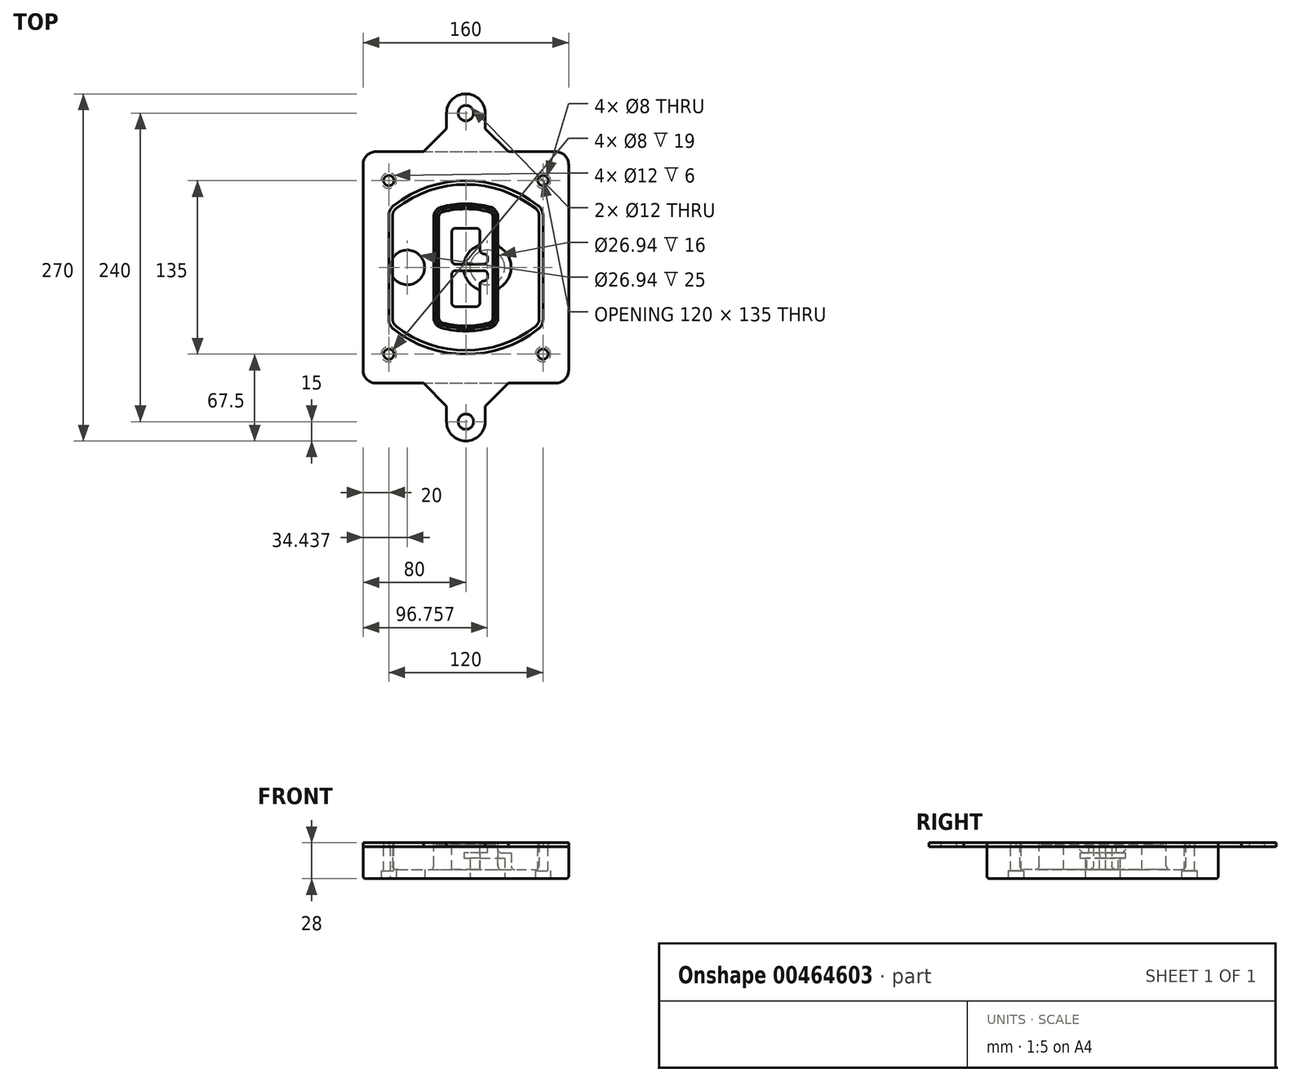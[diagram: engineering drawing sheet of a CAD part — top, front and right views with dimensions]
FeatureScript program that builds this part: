
annotation { "Feature Type Name" : "Feature", "Feature Type Description" : "" }
export const myFeature = defineFeature(function(context is Context, id is Id, definition is map)
    precondition{}
    {
        {
            var Q0;
            Q0=qCreatedBy(makeId("Top.planeOp"),FACE);
            var sketch = newSketch(context, id + "F0", { "sketchPlane" : qUnion([Q0])});
            skPoint(sketch, "E0.rect.middle", {"position": v(0, 0) * mm});
            skLineSegment(sketch, "E1.bottom", {"start": v(-70, -90) * mm, "end": v(70, -90) * mm});
            skLineSegment(sketch, "E1.top", {"start": v(-70, 90) * mm, "end": v(70, 90) * mm});
            skLineSegment(sketch, "E1.left", {"start": v(-80, -80) * mm, "end": v(-80, 80) * mm});
            skLineSegment(sketch, "E1.right", {"start": v(80, -80) * mm, "end": v(80, 80) * mm});
            skLineSegment(sketch, "E2", {"start": v(-80, 90) * mm, "end": v(80, -90) * mm, "construction": true});
            skLineSegment(sketch, "E3", {"start": v(80, 90) * mm, "end": v(-80, -90) * mm, "construction": true});
            skCircle(sketch, "E4", {"center": v(-60, 67.5) * mm, "radius": 4 * mm});
            skCircle(sketch, "E5", {"center": v(60, 67.5) * mm, "radius": 4 * mm});
            skCircle(sketch, "E6", {"center": v(60, -67.5) * mm, "radius": 4 * mm});
            skCircle(sketch, "E7", {"center": v(-60, -67.5) * mm, "radius": 4 * mm});
            skLineSegment(sketch, "E8", {"start": v(-60, 67.5) * mm, "end": v(60, 67.5) * mm, "construction": true});
            skLineSegment(sketch, "E9", {"start": v(60, 67.5) * mm, "end": v(60, -67.5) * mm, "construction": true});
            skLineSegment(sketch, "E10", {"start": v(60, -67.5) * mm, "end": v(-60, -67.5) * mm, "construction": true});
            skLineSegment(sketch, "E11", {"start": v(-60, -67.5) * mm, "end": v(-60, 67.5) * mm, "construction": true});
            skLineSegment(sketch, "E12", {"start": v(-60, 40.3) * mm, "end": v(-60, -40.3) * mm});
            skLineSegment(sketch, "E13", {"start": v(60, 40.3) * mm, "end": v(60, -40.3) * mm});
            skArc(sketch, "E14", {"start": v(56.15, 48.18) * mm, "mid": v(0, 67.5) * mm, "end": v(-56.15, 48.18) * mm});
            skArc(sketch, "E15", {"start": v(-56.15, -48.18) * mm, "mid": v(0, -67.5) * mm, "end": v(56.15, -48.18) * mm});
            skLineSegment(sketch, "E16", {"start": v(-60, 0) * mm, "end": v(60, 0) * mm, "construction": true});
            skPoint(sketch, "E17.visualSharp", {"position": v(-60, -45) * mm});
            skArc(sketch, "E17.filletArc", {"start": v(-60, -40.3) * mm, "mid": v(-58.99, -44.68) * mm, "end": v(-56.15, -48.18) * mm});
            skPoint(sketch, "E18.visualSharp", {"position": v(-60, 45) * mm});
            skArc(sketch, "E18.filletArc", {"start": v(-56.15, 48.18) * mm, "mid": v(-58.99, 44.68) * mm, "end": v(-60, 40.3) * mm});
            skPoint(sketch, "E19.visualSharp", {"position": v(60, 45) * mm});
            skArc(sketch, "E19.filletArc", {"start": v(60, 40.3) * mm, "mid": v(58.99, 44.68) * mm, "end": v(56.15, 48.18) * mm});
            skPoint(sketch, "E20.visualSharp", {"position": v(60, -45) * mm});
            skArc(sketch, "E20.filletArc", {"start": v(56.15, -48.18) * mm, "mid": v(58.99, -44.68) * mm, "end": v(60, -40.3) * mm});
            skPoint(sketch, "E21.visualSharp", {"position": v(-80, 90) * mm});
            skArc(sketch, "E21.filletArc", {"start": v(-70, 90) * mm, "mid": v(-77.07, 87.07) * mm, "end": v(-80, 80) * mm});
            skPoint(sketch, "E22.visualSharp", {"position": v(80, 90) * mm});
            skArc(sketch, "E22.filletArc", {"start": v(80, 80) * mm, "mid": v(77.07, 87.07) * mm, "end": v(70, 90) * mm});
            skPoint(sketch, "E23.visualSharp", {"position": v(80, -90) * mm});
            skArc(sketch, "E23.filletArc", {"start": v(70, -90) * mm, "mid": v(77.07, -87.07) * mm, "end": v(80, -80) * mm});
            skPoint(sketch, "E24.visualSharp", {"position": v(-80, -90) * mm});
            skArc(sketch, "E24.filletArc", {"start": v(-80, -80) * mm, "mid": v(-77.07, -87.07) * mm, "end": v(-70, -90) * mm});
            skArc(sketch, "E25.0", {"start": v(57, 40.3) * mm, "mid": v(56.3, 43.36) * mm, "end": v(54.3, 45.81) * mm});
            skLineSegment(sketch, "E25.1", {"start": v(57, 40.3) * mm, "end": v(57, -40.3) * mm});
            skArc(sketch, "E25.2", {"start": v(54.3, -45.81) * mm, "mid": v(56.3, -43.36) * mm, "end": v(57, -40.3) * mm});
            skArc(sketch, "E25.3", {"start": v(-54.3, -45.81) * mm, "mid": v(0, -64.5) * mm, "end": v(54.3, -45.81) * mm});
            skArc(sketch, "E25.4", {"start": v(-57, -40.3) * mm, "mid": v(-56.3, -43.36) * mm, "end": v(-54.3, -45.81) * mm});
            skArc(sketch, "E25.5", {"start": v(54.3, 45.81) * mm, "mid": v(0, 64.5) * mm, "end": v(-54.3, 45.81) * mm});
            skLineSegment(sketch, "E25.6", {"start": v(-57, 40.3) * mm, "end": v(-57, -40.3) * mm});
            skArc(sketch, "E25.7", {"start": v(-54.3, 45.81) * mm, "mid": v(-56.3, 43.36) * mm, "end": v(-57, 40.3) * mm});
            skArc(sketch, "E26.0", {"start": v(-58.62, 51.33) * mm, "mid": v(-62.58, 46.43) * mm, "end": v(-64, 40.3) * mm});
            skArc(sketch, "E26.1", {"start": v(58.62, 51.33) * mm, "mid": v(0, 71.5) * mm, "end": v(-58.62, 51.33) * mm});
            skArc(sketch, "E26.2", {"start": v(64, 40.3) * mm, "mid": v(62.58, 46.43) * mm, "end": v(58.62, 51.33) * mm});
            skLineSegment(sketch, "E26.3", {"start": v(64, 40.3) * mm, "end": v(64, -40.3) * mm});
            skArc(sketch, "E26.4", {"start": v(58.62, -51.33) * mm, "mid": v(62.58, -46.43) * mm, "end": v(64, -40.3) * mm});
            skLineSegment(sketch, "E26.5", {"start": v(-64, 40.3) * mm, "end": v(-64, -40.3) * mm});
            skArc(sketch, "E26.6", {"start": v(-58.62, -51.33) * mm, "mid": v(0, -71.5) * mm, "end": v(58.62, -51.33) * mm});
            skArc(sketch, "E26.7", {"start": v(-64, -40.3) * mm, "mid": v(-62.58, -46.43) * mm, "end": v(-58.62, -51.33) * mm});
            skSolve(sketch);
        }
        {
            var Q0;
            Q0=makeQuery(id+"F0.imprint","IMPRINT",FACE,{"disambiguationData":[TD([[makeQuery(id+"F0.imprint","IMPRINT",EDGE,{"derivedFrom":sQuery(id+"F0.wireOp",EDGE,"E1.bottom")}),1.0]])]});
            var Q1;
            Q1=makeQuery(id+"F0.imprint","IMPRINT",FACE,{"disambiguationData":[TD([[makeQuery(id+"F0.imprint","IMPRINT",EDGE,{"derivedFrom":sQuery(id+"F0.wireOp",EDGE,"E12")}),1.0]])]});
            var Q2;
            Q2=makeQuery(id+"F0.imprint","IMPRINT",FACE,{"disambiguationData":[TD([[makeQuery(id+"F0.imprint","IMPRINT",EDGE,{"derivedFrom":sQuery(id+"F0.wireOp",EDGE,"E25.0")}),1.0]])]});
            var Q3;
            Q3=makeQuery(id+"F0.imprint","IMPRINT",FACE,{"disambiguationData":[TD([[makeQuery(id+"F0.imprint","IMPRINT",EDGE,{"derivedFrom":sQuery(id+"F0.wireOp",EDGE,"E12")}),-1.0]])]});
            extrude(context, id + "F1", {"entities" : qUnion([Q0, Q1, Q2, Q3]), "oppositeDirection" : true, "depth" : 25 * mm});
        }
        {
            var Q0;
            Q0=makeQuery(id+"F0.imprint","IMPRINT",FACE,{"disambiguationData":[TD([[makeQuery(id+"F0.imprint","IMPRINT",EDGE,{"derivedFrom":sQuery(id+"F0.wireOp",EDGE,"E12")}),1.0]])]});
            extrude(context, id + "F2", {"entities" : qUnion([Q0]), "operationType" : NewBodyOperationType.ADD, "depth" : 3 * mm});
        }
        {
            var Q0;
            Q0=makeQuery(id+"F0.imprint","IMPRINT",FACE,{"disambiguationData":[TD([[makeQuery(id+"F0.imprint","IMPRINT",EDGE,{"derivedFrom":sQuery(id+"F0.wireOp",EDGE,"E25.0")}),1.0]])]});
            extrude(context, id + "F3", {"entities" : qUnion([Q0]), "operationType" : NewBodyOperationType.REMOVE, "oppositeDirection" : true, "depth" : 18 * mm});
        }
        {
            var Q0;
            Q0=makeQuery(id+"F2.opExtrude","CAP_FACE",FACE,{"disambiguationData":[OSD([sQuery(id+"F0.wireOp",EDGE,"E12"),sQuery(id+"F0.wireOp",EDGE,"E13"),sQuery(id+"F0.wireOp",EDGE,"E14"),sQuery(id+"F0.wireOp",EDGE,"E15"),sQuery(id+"F0.wireOp",EDGE,"E17.filletArc"),sQuery(id+"F0.wireOp",EDGE,"E18.filletArc"),sQuery(id+"F0.wireOp",EDGE,"E19.filletArc"),sQuery(id+"F0.wireOp",EDGE,"E20.filletArc"),sQuery(id+"F0.wireOp",EDGE,"E25.0"),sQuery(id+"F0.wireOp",EDGE,"E25.1"),sQuery(id+"F0.wireOp",EDGE,"E25.2"),sQuery(id+"F0.wireOp",EDGE,"E25.3"),sQuery(id+"F0.wireOp",EDGE,"E25.4"),sQuery(id+"F0.wireOp",EDGE,"E25.5"),sQuery(id+"F0.wireOp",EDGE,"E25.6"),sQuery(id+"F0.wireOp",EDGE,"E25.7")])],"isStart":false});
            var sketch = newSketch(context, id + "F4", { "sketchPlane" : qUnion([Q0])});
            skArc(sketch, "E27.0", {"start": v(-19.08, -46.97) * mm, "mid": v(0, -49.5) * mm, "end": v(19.08, -46.97) * mm});
            skArc(sketch, "E28.0", {"start": v(19.08, 46.97) * mm, "mid": v(0, 49.5) * mm, "end": v(-19.08, 46.97) * mm});
            skLineSegment(sketch, "E29", {"start": v(-25, 39.25) * mm, "end": v(-25, -39.25) * mm});
            skLineSegment(sketch, "E30", {"start": v(25, 39.25) * mm, "end": v(25, -39.25) * mm});
            skLineSegment(sketch, "E31", {"start": v(-25, 45.1) * mm, "end": v(25, 45.1) * mm, "construction": true});
            skLineSegment(sketch, "E32", {"start": v(-25, -45.1) * mm, "end": v(25, -45.1) * mm, "construction": true});
            skPoint(sketch, "E33.visualSharp", {"position": v(-25, 45.1) * mm});
            skArc(sketch, "E33.filletArc", {"start": v(-19.08, 46.97) * mm, "mid": v(-23.35, 44.11) * mm, "end": v(-25, 39.25) * mm});
            skPoint(sketch, "E34.visualSharp", {"position": v(25, 45.1) * mm});
            skArc(sketch, "E34.filletArc", {"start": v(25, 39.25) * mm, "mid": v(23.35, 44.11) * mm, "end": v(19.08, 46.97) * mm});
            skPoint(sketch, "E35.visualSharp", {"position": v(25, -45.1) * mm});
            skArc(sketch, "E35.filletArc", {"start": v(19.08, -46.97) * mm, "mid": v(23.35, -44.11) * mm, "end": v(25, -39.25) * mm});
            skPoint(sketch, "E36.visualSharp", {"position": v(-25, -45.1) * mm});
            skArc(sketch, "E36.filletArc", {"start": v(-25, -39.25) * mm, "mid": v(-23.35, -44.11) * mm, "end": v(-19.08, -46.97) * mm});
            skArc(sketch, "E37.0", {"start": v(54.3, 45.81) * mm, "mid": v(0, 64.5) * mm, "end": v(-54.3, 45.81) * mm});
            skArc(sketch, "E37.1", {"start": v(-54.3, 45.81) * mm, "mid": v(-56.3, 43.36) * mm, "end": v(-57, 40.3) * mm});
            skLineSegment(sketch, "E37.2", {"start": v(-57, 40.3) * mm, "end": v(-57, -40.3) * mm});
            skArc(sketch, "E37.3", {"start": v(-57, -40.3) * mm, "mid": v(-56.3, -43.36) * mm, "end": v(-54.3, -45.81) * mm});
            skArc(sketch, "E37.4", {"start": v(-54.3, -45.81) * mm, "mid": v(0, -64.5) * mm, "end": v(54.3, -45.81) * mm});
            skArc(sketch, "E37.5", {"start": v(54.3, -45.81) * mm, "mid": v(56.3, -43.36) * mm, "end": v(57, -40.3) * mm});
            skLineSegment(sketch, "E37.6", {"start": v(57, 40.3) * mm, "end": v(57, -40.3) * mm});
            skArc(sketch, "E37.7", {"start": v(57, 40.3) * mm, "mid": v(56.3, 43.36) * mm, "end": v(54.3, 45.81) * mm});
            skLineSegment(sketch, "E38.0", {"start": v(23, 39.25) * mm, "end": v(23, -39.25) * mm});
            skArc(sketch, "E38.1", {"start": v(18.56, -45.04) * mm, "mid": v(21.76, -42.9) * mm, "end": v(23, -39.25) * mm});
            skArc(sketch, "E38.2", {"start": v(-18.56, -45.04) * mm, "mid": v(0, -47.5) * mm, "end": v(18.56, -45.04) * mm});
            skArc(sketch, "E38.3", {"start": v(-23, -39.25) * mm, "mid": v(-21.76, -42.9) * mm, "end": v(-18.56, -45.04) * mm});
            skLineSegment(sketch, "E38.4", {"start": v(-23, 39.25) * mm, "end": v(-23, -39.25) * mm});
            skArc(sketch, "E38.5", {"start": v(23, 39.25) * mm, "mid": v(21.76, 42.9) * mm, "end": v(18.56, 45.04) * mm});
            skArc(sketch, "E38.6", {"start": v(-18.56, 45.04) * mm, "mid": v(-21.76, 42.9) * mm, "end": v(-23, 39.25) * mm});
            skArc(sketch, "E38.7", {"start": v(18.56, 45.04) * mm, "mid": v(0, 47.5) * mm, "end": v(-18.56, 45.04) * mm});
            skArc(sketch, "E39.0", {"start": v(21, 39.25) * mm, "mid": v(20.18, 41.68) * mm, "end": v(18.04, 43.1) * mm});
            skLineSegment(sketch, "E39.1", {"start": v(21, 39.25) * mm, "end": v(21, -39.25) * mm});
            skArc(sketch, "E39.2", {"start": v(18.04, -43.1) * mm, "mid": v(20.18, -41.68) * mm, "end": v(21, -39.25) * mm});
            skArc(sketch, "E39.3", {"start": v(-18.04, -43.1) * mm, "mid": v(0, -45.5) * mm, "end": v(18.04, -43.1) * mm});
            skArc(sketch, "E39.4", {"start": v(-21, -39.25) * mm, "mid": v(-20.18, -41.68) * mm, "end": v(-18.04, -43.1) * mm});
            skArc(sketch, "E39.5", {"start": v(18.04, 43.1) * mm, "mid": v(0, 45.5) * mm, "end": v(-18.04, 43.1) * mm});
            skLineSegment(sketch, "E39.6", {"start": v(-21, 39.25) * mm, "end": v(-21, -39.25) * mm});
            skArc(sketch, "E39.7", {"start": v(-18.04, 43.1) * mm, "mid": v(-20.18, 41.68) * mm, "end": v(-21, 39.25) * mm});
            skLineSegment(sketch, "E40", {"start": v(-25, 0) * mm, "end": v(25, 0) * mm, "construction": true});
            skLineSegment(sketch, "E41", {"start": v(-11, 5.5) * mm, "end": v(-11, 27.5) * mm});
            skLineSegment(sketch, "E42", {"start": v(-8, 30.5) * mm, "end": v(8, 30.5) * mm});
            skLineSegment(sketch, "E43", {"start": v(11, 27.5) * mm, "end": v(11, 13.5) * mm});
            skLineSegment(sketch, "E44", {"start": v(14, 10.5) * mm, "end": v(14, 10.5) * mm});
            skLineSegment(sketch, "E45", {"start": v(17, 7.5) * mm, "end": v(17, 5.5) * mm});
            skLineSegment(sketch, "E46", {"start": v(14, 2.5) * mm, "end": v(-8, 2.5) * mm});
            skPoint(sketch, "E47.visualSharp", {"position": v(-11, 30.5) * mm});
            skArc(sketch, "E47.filletArc", {"start": v(-8, 30.5) * mm, "mid": v(-10.12, 29.62) * mm, "end": v(-11, 27.5) * mm});
            skPoint(sketch, "E48.visualSharp", {"position": v(11, 30.5) * mm});
            skArc(sketch, "E48.filletArc", {"start": v(11, 27.5) * mm, "mid": v(10.12, 29.62) * mm, "end": v(8, 30.5) * mm});
            skPoint(sketch, "E49.visualSharp", {"position": v(11, 10.5) * mm});
            skArc(sketch, "E49.filletArc", {"start": v(11, 13.5) * mm, "mid": v(11.88, 11.38) * mm, "end": v(14, 10.5) * mm});
            skPoint(sketch, "E50.visualSharp", {"position": v(17, 10.5) * mm});
            skArc(sketch, "E50.filletArc", {"start": v(17, 7.5) * mm, "mid": v(16.12, 9.62) * mm, "end": v(14, 10.5) * mm});
            skPoint(sketch, "E51.visualSharp", {"position": v(17, 2.5) * mm});
            skArc(sketch, "E51.filletArc", {"start": v(14, 2.5) * mm, "mid": v(16.12, 3.38) * mm, "end": v(17, 5.5) * mm});
            skPoint(sketch, "E52.visualSharp", {"position": v(-11, 2.5) * mm});
            skArc(sketch, "E52.filletArc", {"start": v(-11, 5.5) * mm, "mid": v(-10.12, 3.38) * mm, "end": v(-8, 2.5) * mm});
            skLineSegment(sketch, "E53.0.MirrorCS", {"start": v(14, -2.5) * mm, "end": v(-8, -2.5) * mm});
            skArc(sketch, "E54.0.MirrorCS", {"start": v(-11, -5.5) * mm, "mid": v(-10.12, -3.38) * mm, "end": v(-8, -2.5) * mm});
            skLineSegment(sketch, "E55.0.MirrorCS", {"start": v(-11, -5.5) * mm, "end": v(-11, -27.5) * mm});
            skArc(sketch, "E56.0.MirrorCS", {"start": v(-8, -30.5) * mm, "mid": v(-10.12, -29.62) * mm, "end": v(-11, -27.5) * mm});
            skLineSegment(sketch, "E57.0.MirrorCS", {"start": v(-8, -30.5) * mm, "end": v(8, -30.5) * mm});
            skArc(sketch, "E58.0.MirrorCS", {"start": v(11, -27.5) * mm, "mid": v(10.12, -29.62) * mm, "end": v(8, -30.5) * mm});
            skLineSegment(sketch, "E59.0.MirrorCS", {"start": v(11, -27.5) * mm, "end": v(11, -13.5) * mm});
            skArc(sketch, "E60.0.MirrorCS", {"start": v(11, -13.5) * mm, "mid": v(11.88, -11.38) * mm, "end": v(14, -10.5) * mm});
            skArc(sketch, "E61.0.MirrorCS", {"start": v(17, -7.5) * mm, "mid": v(16.12, -9.62) * mm, "end": v(14, -10.5) * mm});
            skLineSegment(sketch, "E62.0.MirrorCS", {"start": v(17, -7.5) * mm, "end": v(17, -5.5) * mm});
            skArc(sketch, "E63.0.MirrorCS", {"start": v(14, -2.5) * mm, "mid": v(16.12, -3.38) * mm, "end": v(17, -5.5) * mm});
            skSolve(sketch);
        }
        {
            var Q0;
            Q0=makeQuery(id+"F4.imprint","IMPRINT",FACE,{"disambiguationData":[TD([[makeQuery(id+"F4.imprint","IMPRINT",EDGE,{"derivedFrom":sQuery(id+"F4.wireOp",EDGE,"E27.0")}),1.0]])]});
            var Q1;
            Q1=makeQuery(id+"F4.imprint","IMPRINT",FACE,{"disambiguationData":[TD([[makeQuery(id+"F4.imprint","IMPRINT",EDGE,{"derivedFrom":sQuery(id+"F4.wireOp",EDGE,"E38.0")}),-1.0]])]});
            var Q2;
            Q2=makeQuery(id+"F4.imprint","IMPRINT",FACE,{"disambiguationData":[TD([[makeQuery(id+"F4.imprint","IMPRINT",EDGE,{"derivedFrom":sQuery(id+"F4.wireOp",EDGE,"E39.0")}),1.0]])]});
            extrude(context, id + "F5", {"entities" : qUnion([Q0, Q1, Q2]), "operationType" : NewBodyOperationType.ADD, "endBound" : BoundingType.UP_TO_NEXT, "oppositeDirection" : true, "depth" : 25 * mm});
        }
        {
            var Q0;
            Q0=makeQuery(id+"F4.imprint","IMPRINT",FACE,{"disambiguationData":[TD([[makeQuery(id+"F4.imprint","IMPRINT",EDGE,{"derivedFrom":sQuery(id+"F4.wireOp",EDGE,"E38.0")}),-1.0]])]});
            extrude(context, id + "F6", {"entities" : qUnion([Q0]), "operationType" : NewBodyOperationType.REMOVE, "oppositeDirection" : true, "depth" : 2 * mm});
        }
        {
            var Q0;
            Q0=makeQuery(id+"F1.opExtrude","CAP_FACE",FACE,{"disambiguationData":[OSD([sQuery(id+"F0.wireOp",EDGE,"E1.bottom"),sQuery(id+"F0.wireOp",EDGE,"E1.top"),sQuery(id+"F0.wireOp",EDGE,"E1.left"),sQuery(id+"F0.wireOp",EDGE,"E1.right"),sQuery(id+"F0.wireOp",EDGE,"E4"),sQuery(id+"F0.wireOp",EDGE,"E5"),sQuery(id+"F0.wireOp",EDGE,"E6"),sQuery(id+"F0.wireOp",EDGE,"E7"),sQuery(id+"F0.wireOp",EDGE,"E21.filletArc"),sQuery(id+"F0.wireOp",EDGE,"E22.filletArc"),sQuery(id+"F0.wireOp",EDGE,"E23.filletArc"),sQuery(id+"F0.wireOp",EDGE,"E24.filletArc")])],"isStart":false});
            var sketch = newSketch(context, id + "F7", { "sketchPlane" : qUnion([Q0])});
            skCircle(sketch, "E64", {"center": v(16.76, 0) * mm, "radius": 13.47 * mm});
            skCircle(sketch, "E65", {"center": v(-45.56, 0) * mm, "radius": 13.47 * mm});
            skLineSegment(sketch, "E66", {"start": v(80, 0) * mm, "end": v(-80, 0) * mm});
            skCircle(sketch, "E67", {"center": v(16.76, 0) * mm, "radius": 18.47 * mm});
            skCircle(sketch, "E68", {"center": v(60, -67.5) * mm, "radius": 6 * mm});
            skCircle(sketch, "E69", {"center": v(-60, -67.5) * mm, "radius": 6 * mm});
            skCircle(sketch, "E70", {"center": v(-60, 67.5) * mm, "radius": 6 * mm});
            skCircle(sketch, "E71", {"center": v(60, 67.5) * mm, "radius": 6 * mm});
            skSolve(sketch);
        }
        {
            var Q0;
            {var subQ1=sQuery(id+"F7.wireOp",EDGE,"E66");var subQ4=sQuery(id+"F7.wireOp",EDGE,"E64");var subQ6=makeQuery(id+"F7.imprint","INTERSECT",VERTEX,{"disambiguationData":[OD(0.0)],"derivedFrom":[subQ4,subQ1]});Q0=makeQuery(id+"F7.imprint","IMPRINT",FACE,{"disambiguationData":[TD([[makeQuery(id+"F7.imprint","IMPRINT",EDGE,{"disambiguationData":[TD([[subQ6,-1.0]])],"derivedFrom":subQ4}),-1.0]])]});}
            var Q1;
            {var subQ0=sQuery(id+"F7.wireOp",EDGE,"E66");var subQ1=sQuery(id+"F7.wireOp",EDGE,"E64");var subQ3=makeQuery(id+"F7.imprint","INTERSECT",VERTEX,{"disambiguationData":[OD(0.0)],"derivedFrom":[subQ1,subQ0]});Q1=makeQuery(id+"F7.imprint","IMPRINT",FACE,{"disambiguationData":[TD([[makeQuery(id+"F7.imprint","IMPRINT",EDGE,{"disambiguationData":[TD([[subQ3,-1.0]])],"derivedFrom":subQ1}),1.0]])]});}
            var Q2;
            {var subQ0=sQuery(id+"F7.wireOp",EDGE,"E66");var subQ1=sQuery(id+"F7.wireOp",EDGE,"E64");var subQ3=makeQuery(id+"F7.imprint","INTERSECT",VERTEX,{"disambiguationData":[OD(0.0)],"derivedFrom":[subQ1,subQ0]});Q2=makeQuery(id+"F7.imprint","IMPRINT",FACE,{"disambiguationData":[TD([[makeQuery(id+"F7.imprint","IMPRINT",EDGE,{"disambiguationData":[TD([[subQ3,1.0]])],"derivedFrom":subQ1}),1.0]])]});}
            var Q3;
            {var subQ1=sQuery(id+"F7.wireOp",EDGE,"E66");var subQ4=sQuery(id+"F7.wireOp",EDGE,"E64");var subQ6=makeQuery(id+"F7.imprint","INTERSECT",VERTEX,{"disambiguationData":[OD(0.0)],"derivedFrom":[subQ4,subQ1]});Q3=makeQuery(id+"F7.imprint","IMPRINT",FACE,{"disambiguationData":[TD([[makeQuery(id+"F7.imprint","IMPRINT",EDGE,{"disambiguationData":[TD([[subQ6,1.0]])],"derivedFrom":subQ4}),-1.0]])]});}
            extrude(context, id + "F8", {"entities" : qUnion([Q0, Q1, Q2, Q3]), "operationType" : NewBodyOperationType.ADD, "oppositeDirection" : true, "depth" : 20 * mm});
        }
        {
            var Q0;
            {var subQ0=sQuery(id+"F7.wireOp",EDGE,"E66");var subQ1=sQuery(id+"F7.wireOp",EDGE,"E64");var subQ3=makeQuery(id+"F7.imprint","INTERSECT",VERTEX,{"disambiguationData":[OD(0.0)],"derivedFrom":[subQ1,subQ0]});Q0=makeQuery(id+"F7.imprint","IMPRINT",FACE,{"disambiguationData":[TD([[makeQuery(id+"F7.imprint","IMPRINT",EDGE,{"disambiguationData":[TD([[subQ3,-1.0]])],"derivedFrom":subQ1}),1.0]])]});}
            var Q1;
            {var subQ0=sQuery(id+"F7.wireOp",EDGE,"E66");var subQ1=sQuery(id+"F7.wireOp",EDGE,"E64");var subQ3=makeQuery(id+"F7.imprint","INTERSECT",VERTEX,{"disambiguationData":[OD(0.0)],"derivedFrom":[subQ1,subQ0]});Q1=makeQuery(id+"F7.imprint","IMPRINT",FACE,{"disambiguationData":[TD([[makeQuery(id+"F7.imprint","IMPRINT",EDGE,{"disambiguationData":[TD([[subQ3,1.0]])],"derivedFrom":subQ1}),1.0]])]});}
            extrude(context, id + "F9", {"entities" : qUnion([Q0, Q1]), "operationType" : NewBodyOperationType.REMOVE, "oppositeDirection" : true, "depth" : 16 * mm});
        }
        {
            var Q0;
            {var subQ0=sQuery(id+"F7.wireOp",EDGE,"E66");var subQ1=sQuery(id+"F7.wireOp",EDGE,"E65");var subQ3=makeQuery(id+"F7.imprint","INTERSECT",VERTEX,{"disambiguationData":[OD(0.0)],"derivedFrom":[subQ1,subQ0]});Q0=makeQuery(id+"F7.imprint","IMPRINT",FACE,{"disambiguationData":[TD([[makeQuery(id+"F7.imprint","IMPRINT",EDGE,{"disambiguationData":[TD([[subQ3,-1.0]])],"derivedFrom":subQ1}),1.0]])]});}
            var Q1;
            {var subQ0=sQuery(id+"F7.wireOp",EDGE,"E66");var subQ1=sQuery(id+"F7.wireOp",EDGE,"E65");var subQ3=makeQuery(id+"F7.imprint","INTERSECT",VERTEX,{"disambiguationData":[OD(0.0)],"derivedFrom":[subQ1,subQ0]});Q1=makeQuery(id+"F7.imprint","IMPRINT",FACE,{"disambiguationData":[TD([[makeQuery(id+"F7.imprint","IMPRINT",EDGE,{"disambiguationData":[TD([[subQ3,1.0]])],"derivedFrom":subQ1}),1.0]])]});}
            extrude(context, id + "F10", {"entities" : qUnion([Q0, Q1]), "operationType" : NewBodyOperationType.REMOVE, "oppositeDirection" : true, "depth" : 25 * mm});
        }
        {
            var Q0;
            Q0=makeQuery(id+"F7.imprint","IMPRINT",FACE,{"disambiguationData":[TD([[makeQuery(id+"F7.imprint","IMPRINT",EDGE,{"derivedFrom":sQuery(id+"F7.wireOp",EDGE,"E68")}),1.0]])]});
            var Q1;
            Q1=makeQuery(id+"F7.imprint","IMPRINT",FACE,{"disambiguationData":[TD([[makeQuery(id+"F7.imprint","IMPRINT",EDGE,{"derivedFrom":makeQuery(id+"F1.opExtrude","CAP_EDGE",EDGE,{"disambiguationData":[OSD([sQuery(id+"F0.wireOp",EDGE,"E5")])],"isStart":false})}),-1.0]])]});
            var Q2;
            Q2=makeQuery(id+"F7.imprint","IMPRINT",FACE,{"disambiguationData":[TD([[makeQuery(id+"F7.imprint","IMPRINT",EDGE,{"derivedFrom":sQuery(id+"F7.wireOp",EDGE,"E69")}),1.0]])]});
            var Q3;
            Q3=makeQuery(id+"F7.imprint","IMPRINT",FACE,{"disambiguationData":[TD([[makeQuery(id+"F7.imprint","IMPRINT",EDGE,{"derivedFrom":makeQuery(id+"F1.opExtrude","CAP_EDGE",EDGE,{"disambiguationData":[OSD([sQuery(id+"F0.wireOp",EDGE,"E4")])],"isStart":false})}),-1.0]])]});
            var Q4;
            Q4=makeQuery(id+"F7.imprint","IMPRINT",FACE,{"disambiguationData":[TD([[makeQuery(id+"F7.imprint","IMPRINT",EDGE,{"derivedFrom":sQuery(id+"F7.wireOp",EDGE,"E70")}),1.0]])]});
            var Q5;
            Q5=makeQuery(id+"F7.imprint","IMPRINT",FACE,{"disambiguationData":[TD([[makeQuery(id+"F7.imprint","IMPRINT",EDGE,{"derivedFrom":makeQuery(id+"F1.opExtrude","CAP_EDGE",EDGE,{"disambiguationData":[OSD([sQuery(id+"F0.wireOp",EDGE,"E7")])],"isStart":false})}),-1.0]])]});
            var Q6;
            Q6=makeQuery(id+"F7.imprint","IMPRINT",FACE,{"disambiguationData":[TD([[makeQuery(id+"F7.imprint","IMPRINT",EDGE,{"derivedFrom":sQuery(id+"F7.wireOp",EDGE,"E71")}),1.0]])]});
            var Q7;
            Q7=makeQuery(id+"F7.imprint","IMPRINT",FACE,{"disambiguationData":[TD([[makeQuery(id+"F7.imprint","IMPRINT",EDGE,{"derivedFrom":makeQuery(id+"F1.opExtrude","CAP_EDGE",EDGE,{"disambiguationData":[OSD([sQuery(id+"F0.wireOp",EDGE,"E6")])],"isStart":false})}),-1.0]])]});
            extrude(context, id + "F11", {"entities" : qUnion([Q0, Q1, Q2, Q3, Q4, Q5, Q6, Q7]), "operationType" : NewBodyOperationType.REMOVE, "oppositeDirection" : true, "depth" : 6 * mm});
        }
        {
            var Q0;
            Q0=makeQuery(id+"F9.boolean.opBoolean","COPY",FACE,{"derivedFrom":makeQuery(id+"F9.opExtrude","CAP_FACE",FACE,{"disambiguationData":[OSD([sQuery(id+"F7.wireOp",EDGE,"E64")])],"isStart":false})});
            var sketch = newSketch(context, id + "F12", { "sketchPlane" : qUnion([Q0])});
            skArc(sketch, "E72.0", {"start": v(11, 17.55) * mm, "mid": v(2.57, 11.82) * mm, "end": v(-1.54, 2.5) * mm});
            skArc(sketch, "E72.1", {"start": v(-1.54, -2.5) * mm, "mid": v(2.57, -11.82) * mm, "end": v(11, -17.55) * mm});
            skLineSegment(sketch, "E73", {"start": v(-1.54, -2.5) * mm, "end": v(14, -2.5) * mm});
            skLineSegment(sketch, "E74.0", {"start": v(14, 2.5) * mm, "end": v(-1.54, 2.5) * mm});
            skArc(sketch, "E74.1", {"start": v(14, 2.5) * mm, "mid": v(16.12, 3.38) * mm, "end": v(17, 5.5) * mm});
            skLineSegment(sketch, "E74.2", {"start": v(17, 7.5) * mm, "end": v(17, 5.5) * mm});
            skArc(sketch, "E74.3", {"start": v(17, 7.5) * mm, "mid": v(16.12, 9.62) * mm, "end": v(14, 10.5) * mm});
            skArc(sketch, "E74.4", {"start": v(11, 13.5) * mm, "mid": v(11.88, 11.38) * mm, "end": v(14, 10.5) * mm});
            skLineSegment(sketch, "E74.5", {"start": v(11, 17.55) * mm, "end": v(11, 13.5) * mm});
            skLineSegment(sketch, "E74.7", {"start": v(14, -2.5) * mm, "end": v(-1.54, -2.5) * mm});
            skArc(sketch, "E74.8", {"start": v(14, -2.5) * mm, "mid": v(16.12, -3.38) * mm, "end": v(17, -5.5) * mm});
            skLineSegment(sketch, "E74.9", {"start": v(17, -7.5) * mm, "end": v(17, -5.5) * mm});
            skArc(sketch, "E74.10", {"start": v(17, -7.5) * mm, "mid": v(16.12, -9.62) * mm, "end": v(14, -10.5) * mm});
            skArc(sketch, "E74.11", {"start": v(11, -13.5) * mm, "mid": v(11.88, -11.38) * mm, "end": v(14, -10.5) * mm});
            skLineSegment(sketch, "E74.12", {"start": v(11, -17.55) * mm, "end": v(11, -13.5) * mm});
            skPoint(sketch, "E75.orphan", {"position": v(11, -27.5) * mm});
            skPoint(sketch, "E76.orphan", {"position": v(-8, -2.5) * mm});
            skPoint(sketch, "E77.orphan", {"position": v(-8, 2.5) * mm});
            skPoint(sketch, "E78.orphan", {"position": v(11, 27.5) * mm});
            skSolve(sketch);
        }
        {
            var Q0;
            {var subQ7=sQuery(id+"F12.wireOp",EDGE,"E72.0");var subQ14=sQuery(id+"F12.wireOp",EDGE,"E72.1");var subQ16=sQuery(id+"F12.wireOp",EDGE,"E74.1");var subQ18=sQuery(id+"F12.wireOp",EDGE,"E74.8");Q0=qUnion([makeQuery(id+"F12.imprint","IMPRINT",FACE,{"disambiguationData":[TD([[makeQuery(id+"F12.imprint","IMPRINT",EDGE,{"derivedFrom":subQ7}),1.0]])]}),makeQuery(id+"F12.imprint","IMPRINT",FACE,{"disambiguationData":[TD([[makeQuery(id+"F12.imprint","IMPRINT",EDGE,{"derivedFrom":subQ14}),1.0]])]}),makeQuery(id+"F12.imprint","IMPRINT",FACE,{"disambiguationData":[TD([[makeQuery(id+"F12.imprint","IMPRINT",EDGE,{"derivedFrom":subQ16}),1.0]])]}),makeQuery(id+"F12.imprint","IMPRINT",FACE,{"disambiguationData":[TD([[makeQuery(id+"F12.imprint","IMPRINT",EDGE,{"derivedFrom":subQ18}),-1.0]])]})]);}
            var Q1;
            Q1=makeQuery(id+"F5.boolean.opBoolean","SPLIT",FACE,{"disambiguationData":[TD([makeQuery(id+"F5.opExtrude","SWEPT_FACE",FACE,{"disambiguationData":[OSD([sQuery(id+"F4.wireOp",EDGE,"E41")])]})])],"derivedFrom":makeQuery(id+"F3.boolean.opBoolean","COPY",FACE,{"derivedFrom":makeQuery(id+"F3.opExtrude","CAP_FACE",FACE,{"disambiguationData":[OSD([sQuery(id+"F0.wireOp",EDGE,"E25.0"),sQuery(id+"F0.wireOp",EDGE,"E25.1"),sQuery(id+"F0.wireOp",EDGE,"E25.2"),sQuery(id+"F0.wireOp",EDGE,"E25.3"),sQuery(id+"F0.wireOp",EDGE,"E25.4"),sQuery(id+"F0.wireOp",EDGE,"E25.5"),sQuery(id+"F0.wireOp",EDGE,"E25.6"),sQuery(id+"F0.wireOp",EDGE,"E25.7")])],"isStart":false})})});
            extrude(context, id + "F13", {"entities" : qUnion([Q0]), "operationType" : NewBodyOperationType.REMOVE, "endBound" : BoundingType.UP_TO_SURFACE, "endBoundEntityFace" : qUnion([Q1]), "depth" : 25 * mm});
        }
        {
            var Q0;
            Q0=makeQuery(id+"F3.boolean.opBoolean","COPY",EDGE,{"derivedFrom":makeQuery(id+"F3.opExtrude","CAP_EDGE",EDGE,{"disambiguationData":[OSD([sQuery(id+"F0.wireOp",EDGE,"E25.6")])],"isStart":false})});
            var Q1;
            Q1=makeQuery(id+"F8.boolean.opBoolean","INTERSECT",EDGE,{"derivedFrom":[makeQuery(id+"F5.opExtrude","SWEPT_FACE",FACE,{"disambiguationData":[OSD([sQuery(id+"F4.wireOp",EDGE,"E30")])]}),makeQuery(id+"F8.opExtrude","CAP_FACE",FACE,{"disambiguationData":[OSD([sQuery(id+"F7.wireOp",EDGE,"E67")])],"isStart":false})]});
            var Q2;
            Q2=makeQuery(id+"F8.boolean.opBoolean","INTERSECT",EDGE,{"disambiguationData":[OD(1.0)],"derivedFrom":[makeQuery(id+"F5.opExtrude","SWEPT_FACE",FACE,{"disambiguationData":[OSD([sQuery(id+"F4.wireOp",EDGE,"E30")])]}),makeQuery(id+"F8.opExtrude","SWEPT_FACE",FACE,{"disambiguationData":[OSD([sQuery(id+"F7.wireOp",EDGE,"E67")])]})]});
            var Q3;
            {var subQ0=sQuery(id+"F4.wireOp",EDGE,"E30");Q3=makeQuery(id+"F8.boolean.opBoolean","SPLIT",EDGE,{"disambiguationData":[TD([makeQuery(id+"F5.opExtrude","SWEPT_FACE",FACE,{"disambiguationData":[OSD([sQuery(id+"F4.wireOp",EDGE,"E35.filletArc")])]})])],"derivedFrom":makeQuery(id+"F5.opExtrude","CAP_EDGE",EDGE,{"disambiguationData":[OSD([subQ0])],"isStart":false})});}
            var Q4;
            {var subQ0=sQuery(id+"F0.wireOp",EDGE,"E25.7");var subQ1=sQuery(id+"F0.wireOp",EDGE,"E25.1");var subQ2=sQuery(id+"F0.wireOp",EDGE,"E25.6");var subQ3=sQuery(id+"F0.wireOp",EDGE,"E25.5");var subQ4=sQuery(id+"F0.wireOp",EDGE,"E25.4");var subQ5=sQuery(id+"F0.wireOp",EDGE,"E25.0");var subQ6=sQuery(id+"F0.wireOp",EDGE,"E25.2");var subQ7=sQuery(id+"F0.wireOp",EDGE,"E25.3");Q4=makeQuery(id+"F8.boolean.opBoolean","INTERSECT",EDGE,{"derivedFrom":[makeQuery(id+"F5.boolean.opBoolean","SPLIT",FACE,{"disambiguationData":[TD([makeQuery(id+"F2.opExtrude","SWEPT_FACE",FACE,{"disambiguationData":[OSD([subQ5])]})])],"derivedFrom":makeQuery(id+"F3.boolean.opBoolean","COPY",FACE,{"derivedFrom":makeQuery(id+"F3.opExtrude","CAP_FACE",FACE,{"disambiguationData":[OSD([subQ5,subQ1,subQ6,subQ7,subQ4,subQ3,subQ2,subQ0])],"isStart":false})})}),makeQuery(id+"F8.opExtrude","SWEPT_FACE",FACE,{"disambiguationData":[OSD([sQuery(id+"F7.wireOp",EDGE,"E67")])]})]});}
            var Q5;
            Q5=makeQuery(id+"F8.boolean.opBoolean","INTERSECT",EDGE,{"disambiguationData":[OD(0.0)],"derivedFrom":[makeQuery(id+"F5.opExtrude","SWEPT_FACE",FACE,{"disambiguationData":[OSD([sQuery(id+"F4.wireOp",EDGE,"E30")])]}),makeQuery(id+"F8.opExtrude","SWEPT_FACE",FACE,{"disambiguationData":[OSD([sQuery(id+"F7.wireOp",EDGE,"E67")])]})]});
            fillet(context, id + "F14", {"entities" : qUnion([Q0, Q1, Q2, Q3, Q4, Q5]), "radius" : 3 * mm, "tangentPropagation" : true, "allowEdgeOverflow" : false});
        }
        {
            var Q0;
            Q0=makeQuery(id+"F1.opExtrude","CAP_EDGE",EDGE,{"disambiguationData":[OSD([sQuery(id+"F0.wireOp",EDGE,"E1.bottom")])],"isStart":false});
            fillet(context, id + "F15", {"entities" : qUnion([Q0]), "radius" : 2 * mm, "tangentPropagation" : true, "allowEdgeOverflow" : false});
        }
        {
            var Q0;
            {var subQ0=sQuery(id+"F0.wireOp",EDGE,"E21.filletArc");var subQ1=sQuery(id+"F0.wireOp",EDGE,"E7");var subQ2=sQuery(id+"F0.wireOp",EDGE,"E6");var subQ3=sQuery(id+"F0.wireOp",EDGE,"E5");var subQ4=sQuery(id+"F0.wireOp",EDGE,"E4");var subQ5=sQuery(id+"F0.wireOp",EDGE,"E22.filletArc");var subQ6=sQuery(id+"F0.wireOp",EDGE,"E1.bottom");var subQ7=sQuery(id+"F0.wireOp",EDGE,"E1.right");var subQ8=sQuery(id+"F0.wireOp",EDGE,"E1.top");var subQ9=sQuery(id+"F0.wireOp",EDGE,"E1.left");var subQ10=sQuery(id+"F0.wireOp",EDGE,"E23.filletArc");var subQ11=sQuery(id+"F0.wireOp",EDGE,"E24.filletArc");Q0=makeQuery(id+"F2.boolean.opBoolean","SPLIT",FACE,{"disambiguationData":[TD([makeQuery(id+"F1.opExtrude","SWEPT_FACE",FACE,{"disambiguationData":[OSD([subQ6])]})])],"derivedFrom":makeQuery(id+"F1.opExtrude","CAP_FACE",FACE,{"disambiguationData":[OSD([subQ6,subQ8,subQ9,subQ7,subQ4,subQ3,subQ2,subQ1,subQ0,subQ5,subQ10,subQ11])],"isStart":true})});}
            var sketch = newSketch(context, id + "F16", { "sketchPlane" : qUnion([Q0])});
            skLineSegment(sketch, "E79.0.0", {"start": v(70, 90) * mm, "end": v(-70, 90) * mm});
            skArc(sketch, "E79.0.1", {"start": v(-70, 90) * mm, "mid": v(-77.07, 87.07) * mm, "end": v(-80, 80) * mm});
            skLineSegment(sketch, "E79.0.2", {"start": v(-80, 80) * mm, "end": v(-80, -80) * mm});
            skArc(sketch, "E79.0.3", {"start": v(-80, -80) * mm, "mid": v(-77.07, -87.07) * mm, "end": v(-70, -90) * mm});
            skLineSegment(sketch, "E79.0.4", {"start": v(-70, -90) * mm, "end": v(70, -90) * mm});
            skArc(sketch, "E79.0.5", {"start": v(70, -90) * mm, "mid": v(77.07, -87.07) * mm, "end": v(80, -80) * mm});
            skLineSegment(sketch, "E79.0.6", {"start": v(80, -80) * mm, "end": v(80, 80) * mm});
            skArc(sketch, "E79.0.7", {"start": v(80, 80) * mm, "mid": v(77.07, 87.07) * mm, "end": v(70, 90) * mm});
            skCircle(sketch, "E80.0", {"center": v(-60, 67.5) * mm, "radius": 4 * mm});
            skCircle(sketch, "E81.0", {"center": v(-60, -67.5) * mm, "radius": 4 * mm});
            skCircle(sketch, "E82.0", {"center": v(60, -67.5) * mm, "radius": 4 * mm});
            skCircle(sketch, "E83.0", {"center": v(60, 67.5) * mm, "radius": 4 * mm});
            skCircle(sketch, "E84", {"center": v(0, 120) * mm, "radius": 6 * mm});
            skPoint(sketch, "E84.centerSnap0", {"position": v(0, 90) * mm});
            skArc(sketch, "E85", {"start": v(15, 120) * mm, "mid": v(0, 135) * mm, "end": v(-15, 120) * mm});
            skLineSegment(sketch, "E86", {"start": v(0, 120) * mm, "end": v(0, 90) * mm, "construction": true});
            skLineSegment(sketch, "E87", {"start": v(-15, 120) * mm, "end": v(-15, 108) * mm});
            skLineSegment(sketch, "E88", {"start": v(-15, 108) * mm, "end": v(-33, 90) * mm});
            skLineSegment(sketch, "E89", {"start": v(15, 120) * mm, "end": v(15, 108) * mm});
            skLineSegment(sketch, "E90", {"start": v(15, 108) * mm, "end": v(33, 90) * mm});
            skLineSegment(sketch, "E91", {"start": v(-80, 0) * mm, "end": v(80, 0) * mm, "construction": true});
            skArc(sketch, "E92.MirrorCS", {"start": v(15, -120) * mm, "mid": v(0, -135) * mm, "end": v(-15, -120) * mm});
            skLineSegment(sketch, "E93.MirrorCS", {"start": v(-15, -120) * mm, "end": v(-15, -108) * mm});
            skLineSegment(sketch, "E94.MirrorCS", {"start": v(-15, -108) * mm, "end": v(-33, -90) * mm});
            skLineSegment(sketch, "E95.MirrorCS", {"start": v(15, -120) * mm, "end": v(15, -108) * mm});
            skCircle(sketch, "E96.MirrorC", {"center": v(0, -120) * mm, "radius": 6 * mm});
            skLineSegment(sketch, "E97.MirrorCS", {"start": v(15, -108) * mm, "end": v(33, -90) * mm});
            skLineSegment(sketch, "E98.MirrorCS", {"start": v(0, -120) * mm, "end": v(0, -90) * mm, "construction": true});
            skSolve(sketch);
        }
        {
            var Q0;
            Q0=makeQuery(id+"F16.imprint","IMPRINT",FACE,{"disambiguationData":[TD([[makeQuery(id+"F16.imprint","IMPRINT",EDGE,{"derivedFrom":sQuery(id+"F16.wireOp",EDGE,"E84")}),-1.0]])]});
            var Q1;
            Q1=makeQuery(id+"F16.imprint","IMPRINT",FACE,{"disambiguationData":[TD([[makeQuery(id+"F16.imprint","IMPRINT",EDGE,{"derivedFrom":sQuery(id+"F16.wireOp",EDGE,"E93.MirrorCS")}),-1.0]])]});
            var Q2;
            Q2=makeQuery(id+"F16.imprint","IMPRINT",FACE,{"disambiguationData":[TD([[makeQuery(id+"F16.imprint","IMPRINT",EDGE,{"derivedFrom":sQuery(id+"F16.wireOp",EDGE,"E80.0")}),-1.0]])]});
            var Q3;
            Q3=makeQuery(id+"F2.opExtrude","CAP_FACE",FACE,{"disambiguationData":[OSD([sQuery(id+"F0.wireOp",EDGE,"E12"),sQuery(id+"F0.wireOp",EDGE,"E13"),sQuery(id+"F0.wireOp",EDGE,"E14"),sQuery(id+"F0.wireOp",EDGE,"E15"),sQuery(id+"F0.wireOp",EDGE,"E17.filletArc"),sQuery(id+"F0.wireOp",EDGE,"E18.filletArc"),sQuery(id+"F0.wireOp",EDGE,"E19.filletArc"),sQuery(id+"F0.wireOp",EDGE,"E20.filletArc"),sQuery(id+"F0.wireOp",EDGE,"E25.0"),sQuery(id+"F0.wireOp",EDGE,"E25.1"),sQuery(id+"F0.wireOp",EDGE,"E25.2"),sQuery(id+"F0.wireOp",EDGE,"E25.3"),sQuery(id+"F0.wireOp",EDGE,"E25.4"),sQuery(id+"F0.wireOp",EDGE,"E25.5"),sQuery(id+"F0.wireOp",EDGE,"E25.6"),sQuery(id+"F0.wireOp",EDGE,"E25.7")])],"isStart":false});
            extrude(context, id + "F17", {"entities" : qUnion([Q0, Q1, Q2]), "endBound" : BoundingType.UP_TO_SURFACE, "endBoundEntityFace" : qUnion([Q3]), "depth" : 25 * mm});
        }
    });
